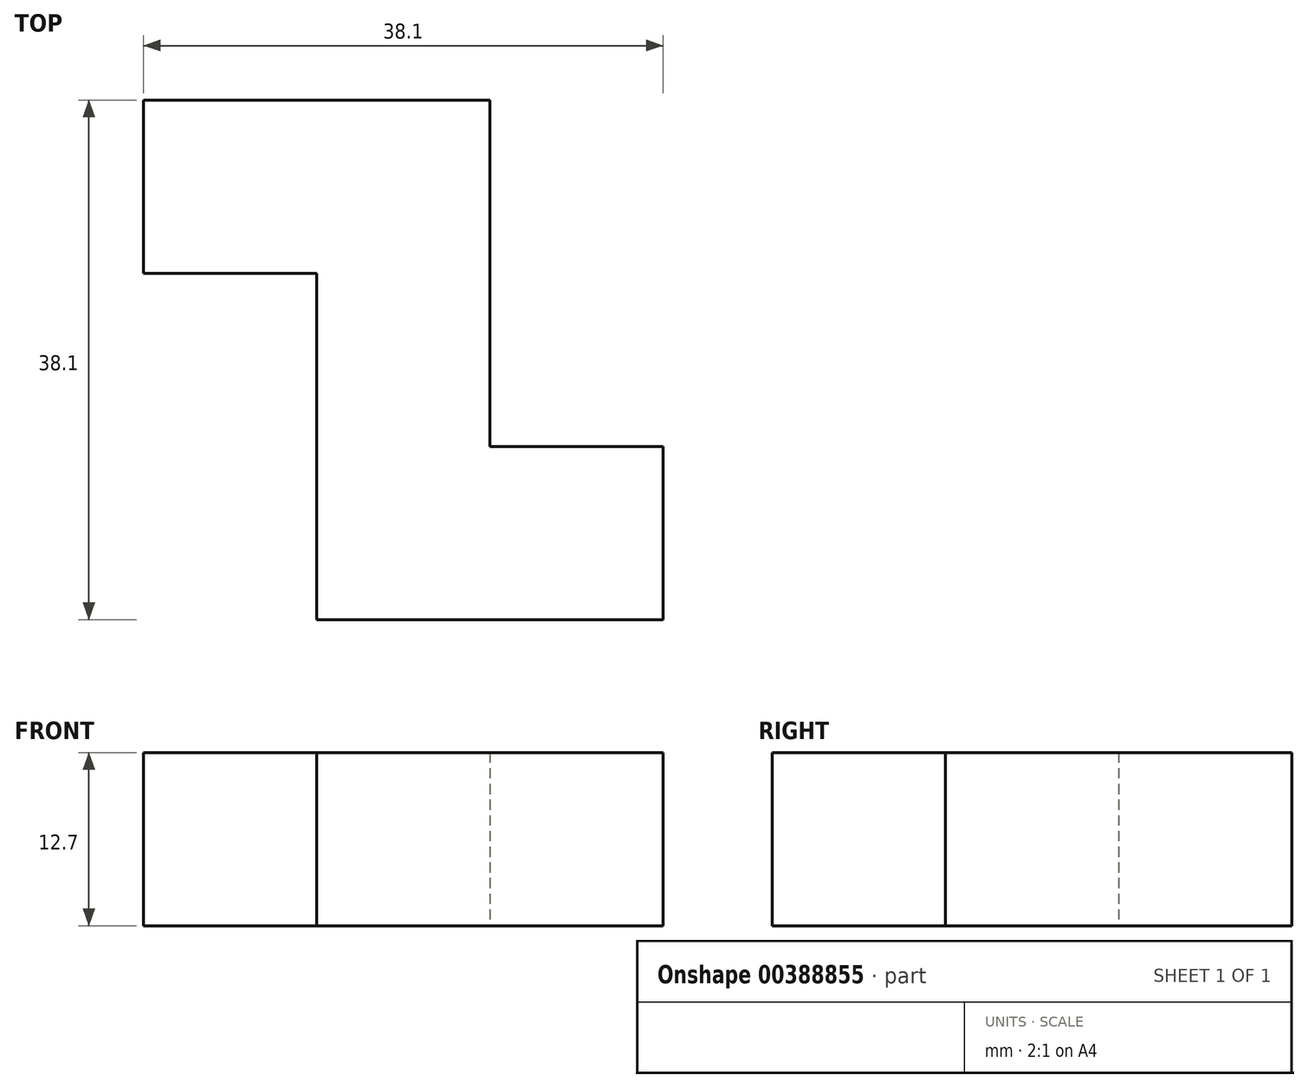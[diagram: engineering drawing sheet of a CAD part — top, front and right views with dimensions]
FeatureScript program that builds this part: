
annotation { "Feature Type Name" : "Feature", "Feature Type Description" : "" }
export const myFeature = defineFeature(function(context is Context, id is Id, definition is map)
    precondition{}
    {
        {
            var Q0;
            Q0=qCreatedBy(makeId("Top.planeOp"),FACE);
            var sketch = newSketch(context, id + "F0", { "sketchPlane" : qUnion([Q0])});
            skLineSegment(sketch, "E0.top", {"start": v(0, 12.7) * mm, "end": v(-25.4, 12.7) * mm});
            skLineSegment(sketch, "E0.left", {"start": v(0, 0) * mm, "end": v(0, 12.7) * mm});
            skLineSegment(sketch, "E0.right", {"start": v(-25.4, 0) * mm, "end": v(-25.4, 12.7) * mm});
            skLineSegment(sketch, "E1.left", {"start": v(0, 0) * mm, "end": v(0, -12.7) * mm});
            skLineSegment(sketch, "E1.right", {"start": v(-12.7, 0) * mm, "end": v(-12.7, -12.7) * mm});
            skLineSegment(sketch, "E2.bottom", {"start": v(0, -12.7) * mm, "end": v(12.7, -12.7) * mm});
            skLineSegment(sketch, "E2.top", {"start": v(-12.7, -25.4) * mm, "end": v(12.7, -25.4) * mm});
            skLineSegment(sketch, "E2.left", {"start": v(-12.7, -12.7) * mm, "end": v(-12.7, -25.4) * mm});
            skLineSegment(sketch, "E2.right", {"start": v(12.7, -12.7) * mm, "end": v(12.7, -25.4) * mm});
            skLineSegment(sketch, "E3", {"start": v(-25.4, 0) * mm, "end": v(-12.7, 0) * mm});
            skSolve(sketch);
        }
        {
            var Q0;
            Q0=makeQuery(id+"F0.imprint","IMPRINT",FACE,{"disambiguationData":[TD([[makeQuery(id+"F0.imprint","IMPRINT",EDGE,{"derivedFrom":sQuery(id+"F0.wireOp",EDGE,"E0.top")}),1.0]])]});
            extrude(context, id + "F1", {"entities" : qUnion([Q0]), "depth" : 12.7 * mm});
        }
    });
